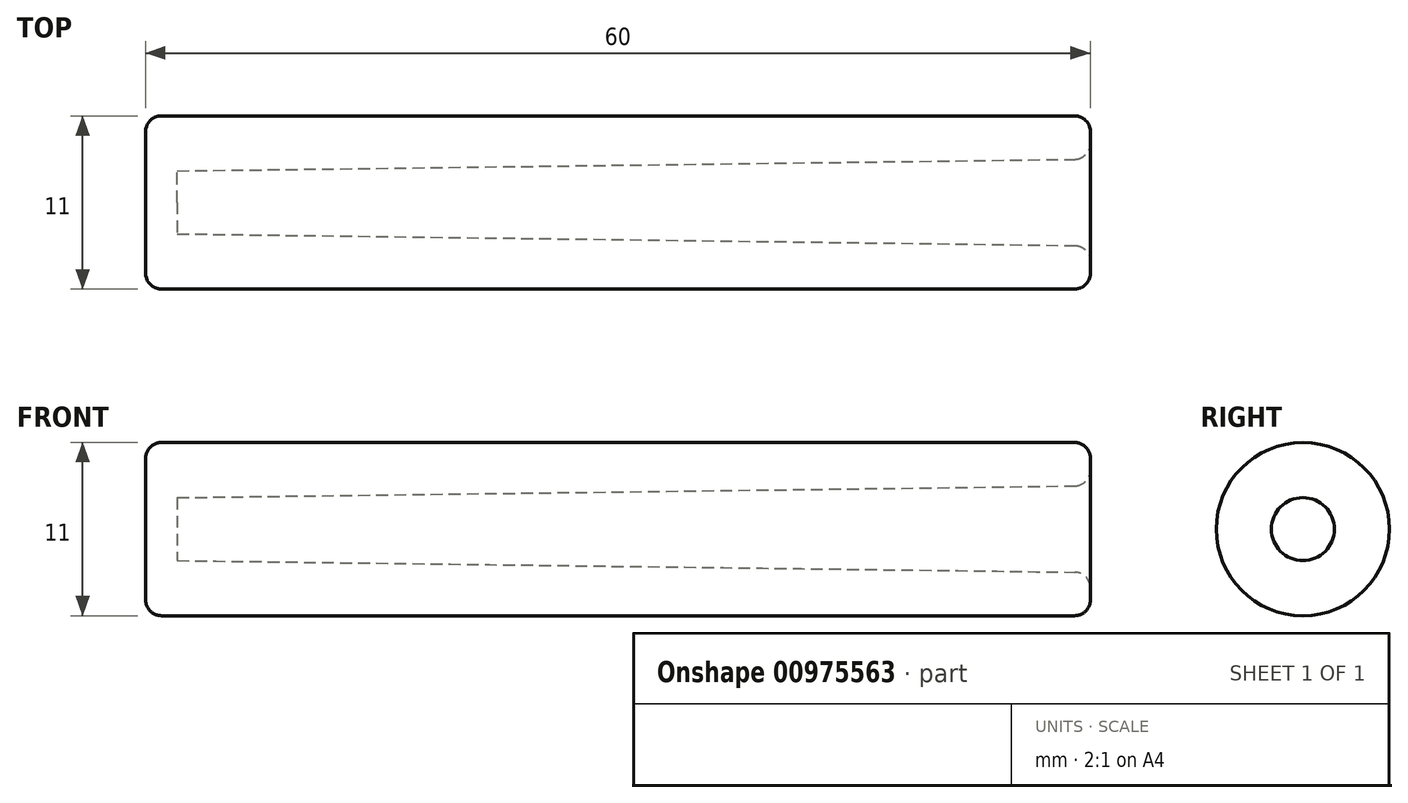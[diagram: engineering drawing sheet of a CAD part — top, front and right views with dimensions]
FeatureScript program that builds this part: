
annotation { "Feature Type Name" : "Feature", "Feature Type Description" : "" }
export const myFeature = defineFeature(function(context is Context, id is Id, definition is map)
    precondition{}
    {
        {
            var Q0;
            Q0=qCreatedBy(makeId("Front.planeOp"),FACE);
            var sketch = newSketch(context, id + "F0", { "sketchPlane" : qUnion([Q0])});
            skLineSegment(sketch, "E0.bottom", {"start": v(-2, 0) * mm, "end": v(0, 0) * mm});
            skLineSegment(sketch, "E0.top", {"start": v(-2, -5.5) * mm, "end": v(0, -5.5) * mm});
            skLineSegment(sketch, "E0.left", {"start": v(-2, 0) * mm, "end": v(-2, -5.5) * mm});
            skLineSegment(sketch, "E0.right", {"start": v(0, 0) * mm, "end": v(0, -5.5) * mm});
            skLineSegment(sketch, "E1", {"start": v(0, -5.5) * mm, "end": v(58, -5.5) * mm});
            skLineSegment(sketch, "E2", {"start": v(58, -5.5) * mm, "end": v(58, -2.75) * mm});
            skLineSegment(sketch, "E3", {"start": v(0, -2) * mm, "end": v(58, -2.75) * mm});
            skSolve(sketch);
        }
        {
            var Q0;
            {var subQ0=sQuery(id+"F0.wireOp",EDGE,"E1");Q0=makeQuery(id+"F0.imprint","IMPRINT",FACE,{"disambiguationData":[TD([[makeQuery(id+"F0.imprint","IMPRINT",EDGE,{"derivedFrom":subQ0}),1.0]])]});}
            var Q1;
            {var subQ1=sQuery(id+"F0.wireOp",EDGE,"E0.bottom");Q1=makeQuery(id+"F0.imprint","IMPRINT",FACE,{"disambiguationData":[TD([[makeQuery(id+"F0.imprint","IMPRINT",EDGE,{"derivedFrom":subQ1}),-1.0]])]});}
            var Q2;
            Q2=sQuery(id+"F0.wireOp",EDGE,"E0.bottom");
            revolve(context, id + "F1", {"surfaceOperationType" : NewSurfaceOperationType.NEW, "entities" : qUnion([Q0, Q1]), "axis" : qUnion([Q2]), "revolveType" : RevolveType.FULL});
        }
        {
            var Q0;
            Q0=makeQuery(id+"F1.opRevolve","SWEPT_FACE",FACE,{"disambiguationData":[OSD([sQuery(id+"F0.wireOp",EDGE,"E0.top"),sQuery(id+"F0.wireOp",EDGE,"E1")])]});
            var Q1;
            Q1=makeQuery(id+"F1.opRevolve","SWEPT_EDGE",EDGE,{"disambiguationData":[OSD([sQuery(id+"F0.wireOp",EDGE,"E1"),sQuery(id+"F0.wireOp",EDGE,"E2")])]});
            var Q2;
            Q2=makeQuery(id+"F1.opRevolve","SWEPT_EDGE",EDGE,{"disambiguationData":[OSD([sQuery(id+"F0.wireOp",EDGE,"E2"),sQuery(id+"F0.wireOp",EDGE,"E3")])]});
            fillet(context, id + "F2", {"entities" : qUnion([Q0, Q1, Q2]), "radius" : 1 * mm, "tangentPropagation" : true, "allowEdgeOverflow" : false});
        }
    });
